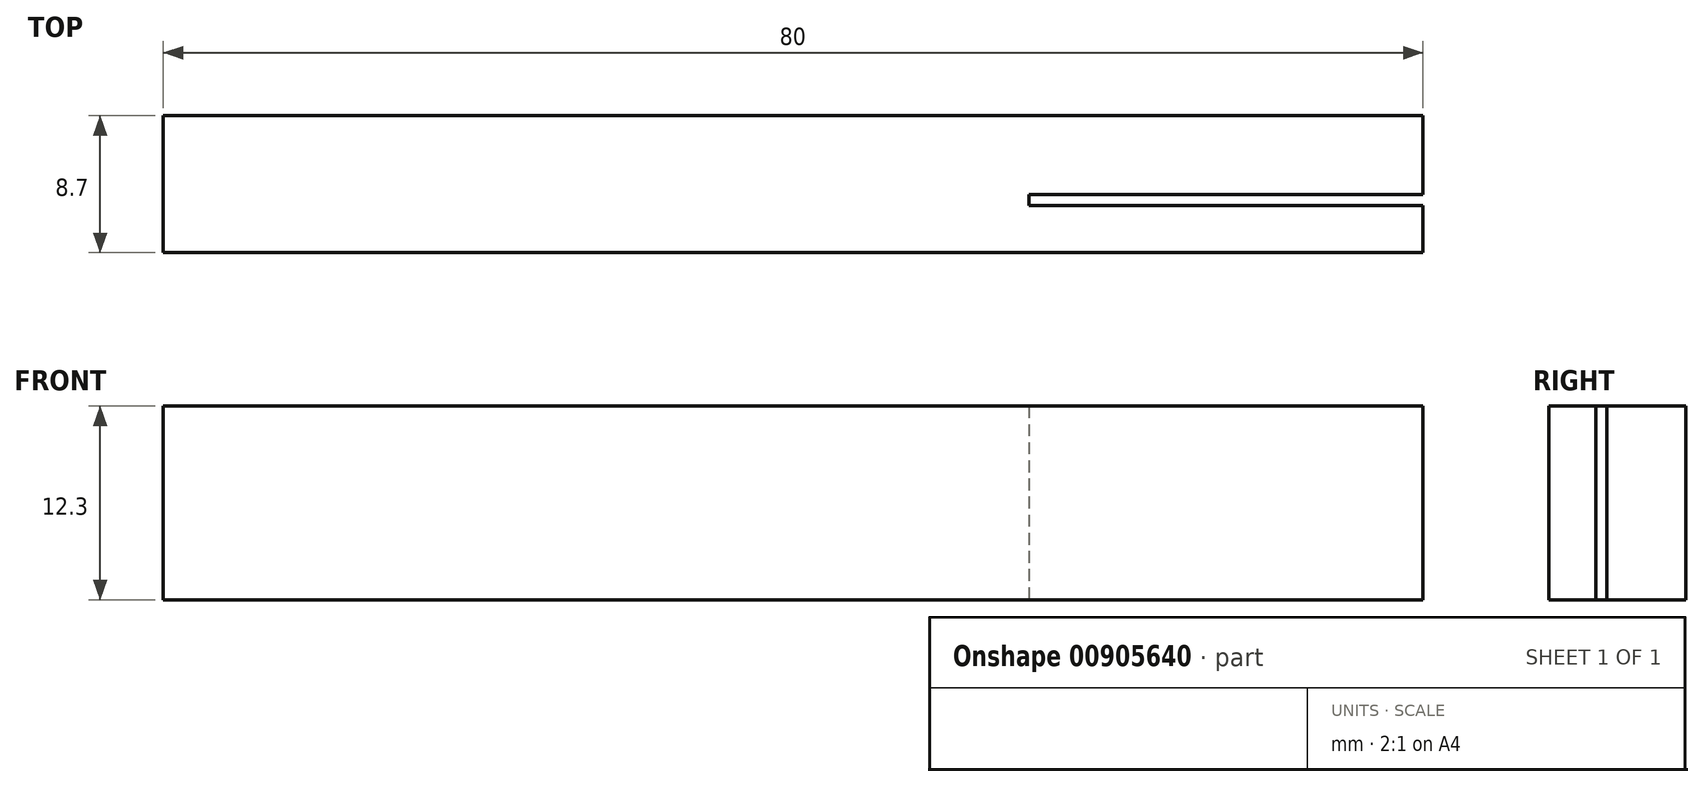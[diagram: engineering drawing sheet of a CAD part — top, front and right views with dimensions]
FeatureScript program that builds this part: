
annotation { "Feature Type Name" : "Feature", "Feature Type Description" : "" }
export const myFeature = defineFeature(function(context is Context, id is Id, definition is map)
    precondition{}
    {
        {
            var Q0;
            Q0=qCreatedBy(makeId("Front.planeOp"),FACE);
            var sketch = newSketch(context, id + "F0", { "sketchPlane" : qUnion([Q0])});
            skLineSegment(sketch, "E0", {"start": v(-56.35, 0) * mm, "end": v(-56.35, 8.7) * mm});
            skLineSegment(sketch, "E1", {"start": v(-56.35, 8.7) * mm, "end": v(-6.35, 8.7) * mm});
            skLineSegment(sketch, "E2", {"start": v(-6.35, 8.7) * mm, "end": v(23.65, 8.7) * mm});
            skLineSegment(sketch, "E3", {"start": v(23.65, 0) * mm, "end": v(-56.35, 0) * mm});
            skLineSegment(sketch, "E4", {"start": v(23.65, 0) * mm, "end": v(23.65, 3) * mm});
            skLineSegment(sketch, "E5", {"start": v(23.65, 3) * mm, "end": v(-1.35, 3) * mm});
            skLineSegment(sketch, "E6", {"start": v(-1.35, 3) * mm, "end": v(-1.35, 3.7) * mm});
            skLineSegment(sketch, "E7", {"start": v(-1.35, 3.7) * mm, "end": v(23.65, 3.7) * mm});
            skLineSegment(sketch, "E8", {"start": v(23.65, 3.7) * mm, "end": v(23.65, 8.7) * mm});
            skLineSegment(sketch, "E9.bottom", {"start": v(23.65, 3.7) * mm, "end": v(23.05, 3.7) * mm});
            skLineSegment(sketch, "E9.top", {"start": v(23.65, 3) * mm, "end": v(23.05, 3) * mm});
            skLineSegment(sketch, "E9.left", {"start": v(23.65, 3.7) * mm, "end": v(23.65, 3) * mm});
            skLineSegment(sketch, "E9.right", {"start": v(23.05, 3.7) * mm, "end": v(23.05, 3) * mm});
            skLineSegment(sketch, "E10.bottom", {"start": v(13.09, 3.7) * mm, "end": v(13.69, 3.7) * mm});
            skLineSegment(sketch, "E10.top", {"start": v(13.09, 3) * mm, "end": v(13.69, 3) * mm});
            skLineSegment(sketch, "E10.left", {"start": v(13.09, 3.7) * mm, "end": v(13.09, 3) * mm});
            skLineSegment(sketch, "E10.right", {"start": v(13.69, 3.7) * mm, "end": v(13.69, 3) * mm});
            skLineSegment(sketch, "E11.bottom", {"start": v(4.04, 3.7) * mm, "end": v(4.64, 3.7) * mm});
            skLineSegment(sketch, "E11.top", {"start": v(4.04, 3) * mm, "end": v(4.64, 3) * mm});
            skLineSegment(sketch, "E11.left", {"start": v(4.04, 3.7) * mm, "end": v(4.04, 3) * mm});
            skLineSegment(sketch, "E11.right", {"start": v(4.64, 3.7) * mm, "end": v(4.64, 3) * mm});
            skSolve(sketch);
        }
        {
            var Q0;
            Q0=makeQuery(id+"F0.imprint","IMPRINT",FACE,{"disambiguationData":[TD([[makeQuery(id+"F0.imprint","IMPRINT",EDGE,{"derivedFrom":sQuery(id+"F0.wireOp",EDGE,"E0")}),-1.0]])]});
            extrude(context, id + "F1", {"entities" : qUnion([Q0]), "depth" : 12.3 * mm, "offsetDistance" : 25 * mm});
        }
        {
            var Q0;
            Q0=makeQuery(id+"F1.opExtrude","SWEPT_BODY",BODY,{"disambiguationData":[OSD([sQuery(id+"F0.wireOp",EDGE,"E0"),sQuery(id+"F0.wireOp",EDGE,"E1"),sQuery(id+"F0.wireOp",EDGE,"E2"),sQuery(id+"F0.wireOp",EDGE,"E3"),sQuery(id+"F0.wireOp",EDGE,"E4"),sQuery(id+"F0.wireOp",EDGE,"E5"),sQuery(id+"F0.wireOp",EDGE,"E6"),sQuery(id+"F0.wireOp",EDGE,"E7"),sQuery(id+"F0.wireOp",EDGE,"E8"),sQuery(id+"F0.wireOp",EDGE,"E9.bottom"),sQuery(id+"F0.wireOp",EDGE,"E9.top"),sQuery(id+"F0.wireOp",EDGE,"E10.bottom"),sQuery(id+"F0.wireOp",EDGE,"E10.top"),sQuery(id+"F0.wireOp",EDGE,"E11.bottom"),sQuery(id+"F0.wireOp",EDGE,"E11.top")])]});
            var Q1;
            Q1=makeQuery(id+"F1.opExtrude","CAP_EDGE",EDGE,{"disambiguationData":[OSD([sQuery(id+"F0.wireOp",EDGE,"E3")])],"isStart":false});
            transform(context, id + "F2", {"entities" : qUnion([Q0]), "transformType" : TransformType.ROTATION, "transformAxis" : qUnion([Q1]), "angle" : 90 * degree, "makeCopy" : false});
        }
    });
